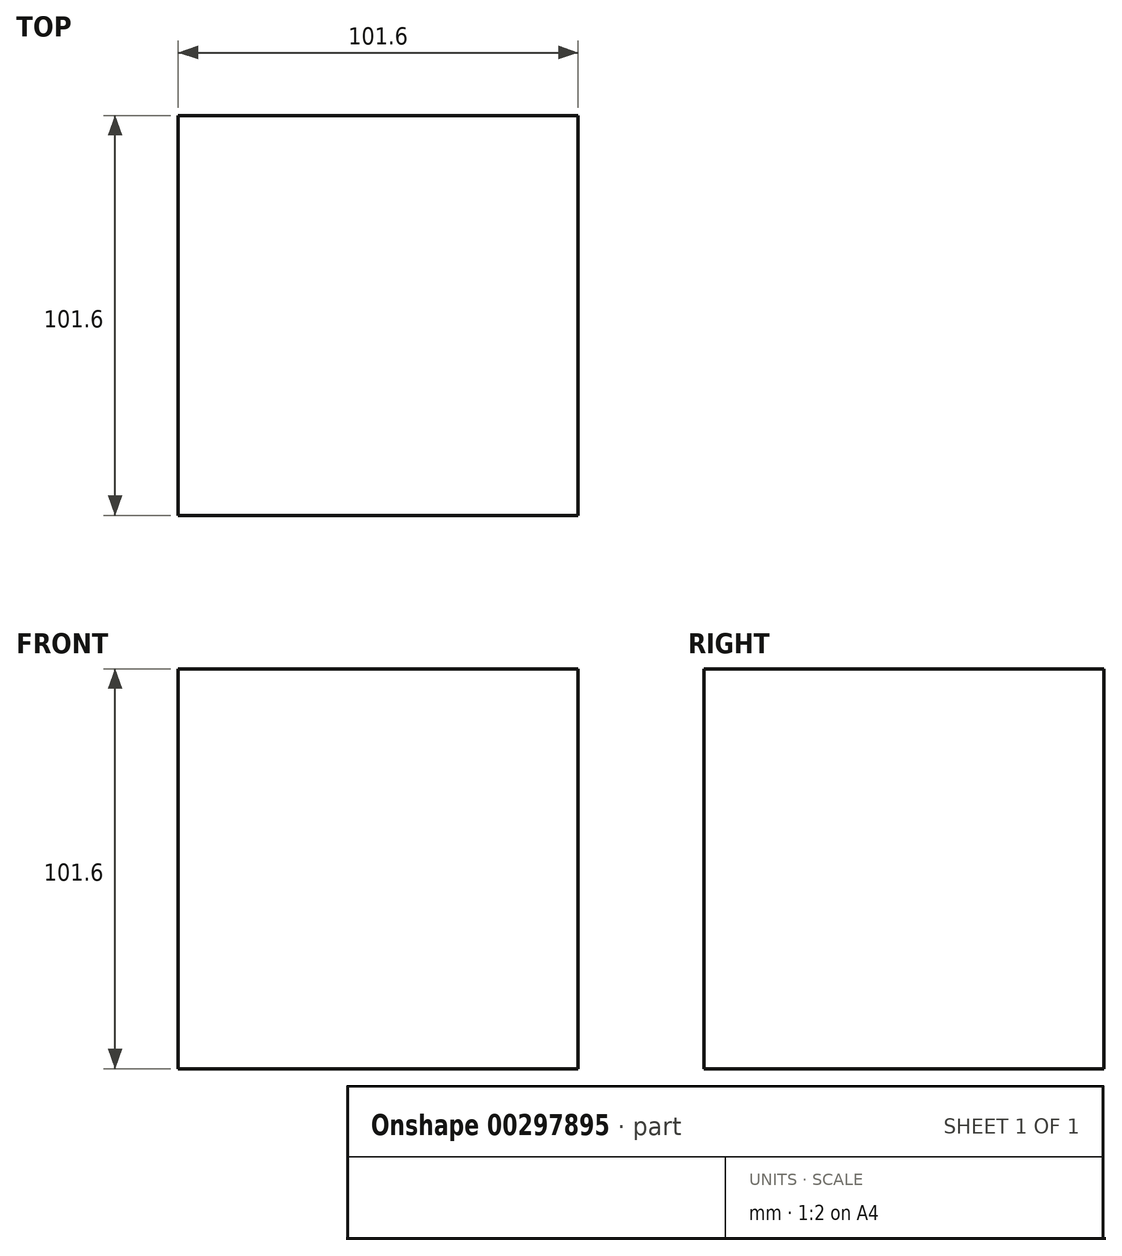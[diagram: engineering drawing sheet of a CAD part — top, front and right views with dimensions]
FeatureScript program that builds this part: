
annotation { "Feature Type Name" : "Feature", "Feature Type Description" : "" }
export const myFeature = defineFeature(function(context is Context, id is Id, definition is map)
    precondition{}
    {
        {
            var Q0;
            Q0=qCreatedBy(makeId("Front.planeOp"),FACE);
            var sketch = newSketch(context, id + "F0", { "sketchPlane" : qUnion([Q0])});
            skLineSegment(sketch, "E0.bottom", {"start": v(101.6, 101.6) * mm, "end": v(0, 101.6) * mm});
            skLineSegment(sketch, "E0.top", {"start": v(101.6, 0) * mm, "end": v(0, 0) * mm});
            skLineSegment(sketch, "E0.left", {"start": v(101.6, 101.6) * mm, "end": v(101.6, 0) * mm});
            skLineSegment(sketch, "E0.right", {"start": v(0, 101.6) * mm, "end": v(0, 0) * mm});
            skSolve(sketch);
        }
        {
            var Q0;
            Q0 = qSketchRegion(id + "F0", true);
            extrude(context, id + "F1", {"entities" : qUnion([Q0]), "depth" : 101.6 * mm});
        }
    });
